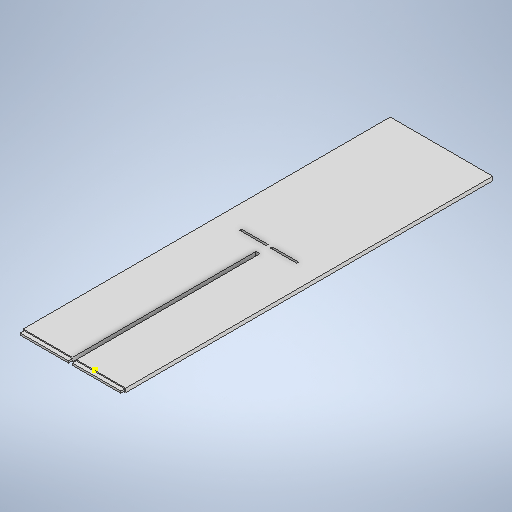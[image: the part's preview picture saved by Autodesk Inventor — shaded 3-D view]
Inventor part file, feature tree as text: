
AUTODESK INVENTOR PART (.ipt)
format: ipt  version: 2025.2 (Build 292293000, 293)  size: 408,064 bytes
history: native  units: mm
features: sketch x15, extrude x14, projected_geometry x3
ambient origin geometry x8: Origin, YZ Plane, XZ Plane, XY Plane, X Axis, Y Axis, Z Axis, Center Point
bodies: Solid1 (feature_tree)
feature tree (32):
  extrude  "Extrusion1"  Depth=447.675mm
  extrude  "Extrusion2"  Depth=4.7625mm TaperAngle=0.0deg
  extrude  "Extrusion3"  Depth=10.0mm TaperAngle=0.0deg
  extrude  "Extrusion4"  Depth=158.838mm TaperAngle=0.0deg
  sketch  "Sketch5"  dims[d25=4.763mm d26=223.837mm d27=0.0mm]
  extrude  "Extrusion5"  Depth=223.837mm TaperAngle=0.0deg
  extrude  "Extrusion6"  Depth=15.0mm TaperAngle=0.0deg
  extrude  "Extrusion7"  Depth=2.374mm TaperAngle=0.0deg
  extrude  "Extrusion8"  Depth=2.374mm TaperAngle=0.0deg
  extrude  "Extrusion9"  Depth=4.763mm
  extrude  "Extrusion10"  Depth=10.0mm TaperAngle=0.0deg
  extrude  "Extrusion11"  Depth=10.0mm TaperAngle=0.0deg
  extrude  "Extrusion12"  [1 undecoded]
  extrude  "Extrusion13"  [1 undecoded]
  extrude  "Extrusion14"  [1 undecoded]
  sketch  "Sketch1"  dims[d0=50.0mm d1=447.675mm]
  sketch  "Sketch2"  dims[d2=4.7625mm d3=0.0mm d9=4.7625mm d10=0.0mm]
  sketch  "Sketch3"  dims[d11=25.0mm d18=10.0mm d19=0.0mm]
  sketch  "Sketch4"  dims[d20=10.0mm d21=0.0mm d22=158.838mm d23=0.0mm]
  sketch  "Sketch6"  dims[d28=15.0mm d29=0.0mm d30=15.0mm d31=0.0mm]
  projected_geometry  "Projected Loop1"
  sketch  "Sketch8"  dims[d35=2.374mm d36=10.0mm d37=0.0mm]
  sketch  "Sketch9"  dims[d43=2.374mm d44=10.0mm d45=0.0mm]
  projected_geometry  "Projected Loop2"
  sketch  "Sketch10"  dims[d46=4.763mm d47=0.0mm d48=37.5mm]
  projected_geometry  "Projected Loop3"
  sketch  "Sketch14"  dims[d49=37.5mm d50=10.0mm d51=0.0mm]
  sketch  "Sketch17"  dims[d53=10.0mm d54=0.0mm d57=10.0mm d58=0.0mm]
  sketch  "Sketch18"
  sketch  "Sketch19"
  sketch  "Sketch20"
  sketch  "Sketch21"
note: 3 required parameter values undecoded (feature->parameter linkage not recoverable at this tier; creation-order binding heuristic only, values carry confidence <= 0.55)
